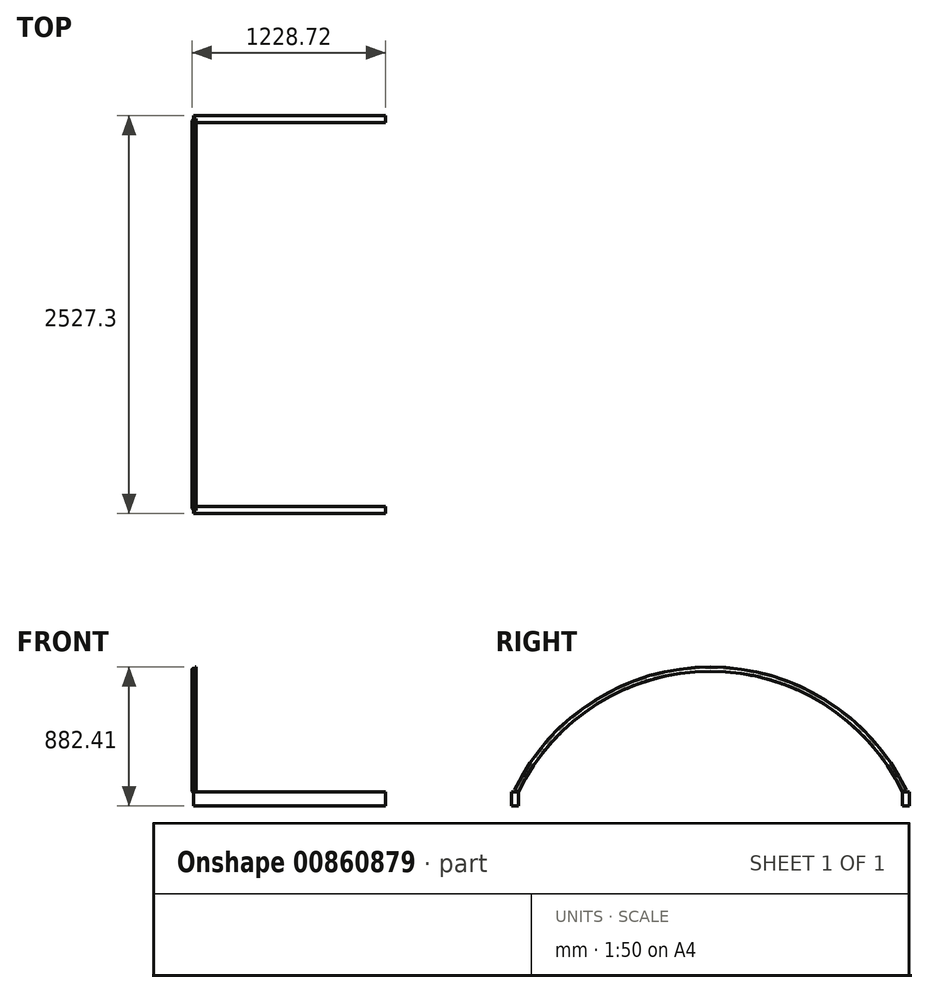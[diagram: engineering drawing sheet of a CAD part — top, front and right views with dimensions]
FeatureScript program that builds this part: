
annotation { "Feature Type Name" : "Feature", "Feature Type Description" : "" }
export const myFeature = defineFeature(function(context is Context, id is Id, definition is map)
    precondition{}
    {
        {
            var Q0;
            Q0=qCreatedBy(makeId("Top.planeOp"),FACE);
            var sketch = newSketch(context, id + "F0", { "sketchPlane" : qUnion([Q0])});
            skLineSegment(sketch, "E0", {"start": v(-3470.7, 1219.2) * mm, "end": v(-2251.5, 1219.2) * mm});
            skLineSegment(sketch, "E1.MirrorCS", {"start": v(-3470.7, -1219.2) * mm, "end": v(-2251.5, -1219.2) * mm});
            skLineSegment(sketch, "E2.0", {"start": v(-3470.7, 1263.65) * mm, "end": v(-2251.5, 1263.65) * mm});
            skLineSegment(sketch, "E3", {"start": v(-3470.7, 1219.2) * mm, "end": v(-3470.7, 1263.65) * mm});
            skLineSegment(sketch, "E4", {"start": v(-2251.5, 1219.2) * mm, "end": v(-2251.5, 1263.65) * mm});
            skLineSegment(sketch, "E5.MirrorCS", {"start": v(-3470.7, -1263.65) * mm, "end": v(-2251.5, -1263.65) * mm});
            skLineSegment(sketch, "E6.MirrorCS", {"start": v(-2251.5, -1219.2) * mm, "end": v(-2251.5, -1263.65) * mm});
            skLineSegment(sketch, "E7.MirrorCS", {"start": v(-3470.7, -1219.2) * mm, "end": v(-3470.7, -1263.65) * mm});
            skSolve(sketch);
        }
        {
            var Q0;
            Q0=makeQuery(id+"F0.imprint","IMPRINT",FACE,{"disambiguationData":[TD([[makeQuery(id+"F0.imprint","IMPRINT",EDGE,{"derivedFrom":sQuery(id+"F0.wireOp",EDGE,"E0")}),1.0]])]});
            var Q1;
            Q1=makeQuery(id+"F0.imprint","IMPRINT",FACE,{"disambiguationData":[TD([[makeQuery(id+"F0.imprint","IMPRINT",EDGE,{"derivedFrom":sQuery(id+"F0.wireOp",EDGE,"E1.MirrorCS")}),-1.0]])]});
            extrude(context, id + "F1", {"entities" : qUnion([Q0, Q1]), "depth" : 88.9 * mm, "offsetDistance" : 25.4 * mm});
        }
        {
            var Q0;
            Q0=makeQuery(id+"F1.opExtrude","SWEPT_FACE",FACE,{"disambiguationData":[OSD([sQuery(id+"F0.wireOp",EDGE,"E3")])]});
            var sketch = newSketch(context, id + "F2", { "sketchPlane" : qUnion([Q0])});
            skLineSegment(sketch, "E8.0.0", {"start": v(-1263.65, 0) * mm, "end": v(-1219.2, 0) * mm});
            skLineSegment(sketch, "E8.0.1", {"start": v(-1219.2, 0) * mm, "end": v(-1219.2, 88.9) * mm});
            skLineSegment(sketch, "E8.0.2", {"start": v(-1219.2, 88.9) * mm, "end": v(-1263.65, 88.9) * mm});
            skLineSegment(sketch, "E8.0.3", {"start": v(-1263.65, 88.9) * mm, "end": v(-1263.65, 0) * mm});
            skLineSegment(sketch, "E9.0.0", {"start": v(1219.2, 0) * mm, "end": v(1263.65, 0) * mm});
            skLineSegment(sketch, "E9.0.1", {"start": v(1263.65, 0) * mm, "end": v(1263.65, 88.9) * mm});
            skLineSegment(sketch, "E9.0.2", {"start": v(1263.65, 88.9) * mm, "end": v(1219.2, 88.9) * mm});
            skLineSegment(sketch, "E9.0.3", {"start": v(1219.2, 88.9) * mm, "end": v(1219.2, 0) * mm});
            skArc(sketch, "E10", {"start": v(1219.2, 88.9) * mm, "mid": v(0, 855.1) * mm, "end": v(-1219.2, 88.9) * mm});
            skArc(sketch, "E11.0", {"start": v(1236.36, 97.16) * mm, "mid": v(0, 874.16) * mm, "end": v(-1236.36, 97.16) * mm});
            skLineSegment(sketch, "E12", {"start": v(-1236.36, 97.16) * mm, "end": v(-1219.2, 88.9) * mm});
            skLineSegment(sketch, "E13", {"start": v(1236.36, 97.16) * mm, "end": v(1219.2, 88.9) * mm});
            skSolve(sketch);
        }
        {
            var Q0;
            Q0=sQuery(id+"F2.wireOp",EDGE,"E12");
            cPlane(context, id + "F3", {"entities" : qUnion([Q0]), "cplaneType" : CPlaneType.LINE_ANGLE, "offset" : 25.4 * mm, "angle" : 0 * degree, "width" : 152.4 * mm, "height" : 152.4 * mm});
        }
        {
            var Q0;
            Q0=qCreatedBy(id+"F3.planeOp",FACE);
            var sketch = newSketch(context, id + "F4", { "sketchPlane" : qUnion([Q0])});
            skLineSegment(sketch, "E14.0", {"start": v(-3470.7, -1156.15) * mm, "end": v(-3470.7, -1137.1) * mm});
            skCircle(sketch, "E15", {"center": v(-3470.7, -1146.63) * mm, "radius": 9.53 * mm});
            skSolve(sketch);
        }
        {
            var Q0;
            {var subQ0=sQuery(id+"F4.wireOp",EDGE,"E14.0");Q0=makeQuery(id+"F4.imprint","IMPRINT",FACE,{"disambiguationData":[TD([[makeQuery(id+"F4.imprint","IMPRINT",EDGE,{"derivedFrom":subQ0}),1.0]])]});}
            var Q1;
            {var subQ0=sQuery(id+"F4.wireOp",EDGE,"E14.0");Q1=makeQuery(id+"F4.imprint","IMPRINT",FACE,{"disambiguationData":[TD([[makeQuery(id+"F4.imprint","IMPRINT",EDGE,{"derivedFrom":subQ0}),-1.0]])]});}
            var Q2;
            Q2=sQuery(id+"F2.wireOp",EDGE,"E11.0");
            sweep(context, id + "F5", {"profiles" : qUnion([Q0, Q1]), "path" : qUnion([Q2])});
        }
        {
            var Q0;
            Q0=makeQuery(id+"F2.imprint","IMPRINT",FACE,{"disambiguationData":[TD([[makeQuery(id+"F2.imprint","IMPRINT",EDGE,{"derivedFrom":sQuery(id+"F2.wireOp",EDGE,"E8.0.0")}),-1.0]])]});
            var sketch = newSketch(context, id + "F6", { "sketchPlane" : qUnion([Q0])});
            skLineSegment(sketch, "E16.1.0", {"start": v(1263.65, 88.9) * mm, "end": v(1219.2, 88.9) * mm});
            skLineSegment(sketch, "E16.1.1", {"start": v(1219.2, 88.9) * mm, "end": v(1219.2, 0) * mm});
            skLineSegment(sketch, "E16.1.2", {"start": v(1219.2, 0) * mm, "end": v(1263.65, 0) * mm});
            skLineSegment(sketch, "E16.1.3", {"start": v(1263.65, 0) * mm, "end": v(1263.65, 88.9) * mm});
            skArc(sketch, "E17.0", {"start": v(1236.36, 97.16) * mm, "mid": v(0, 874.16) * mm, "end": v(-1236.36, 97.16) * mm});
            skLineSegment(sketch, "E18", {"start": v(-1259.25, 108.18) * mm, "end": v(-1236.36, 97.16) * mm});
            skLineSegment(sketch, "E19", {"start": v(0, -498) * mm, "end": v(0, 1228.3) * mm, "construction": true});
            skLineSegment(sketch, "E20.anchor1", {"start": v(0, -498) * mm, "end": v(0, 899.56) * mm, "construction": true});
            skLineSegment(sketch, "E21", {"start": v(0, -498) * mm, "end": v(-1259.25, 108.18) * mm, "construction": true});
            skLineSegment(sketch, "E22", {"start": v(0, -498) * mm, "end": v(1259.25, 108.18) * mm, "construction": true});
            skLineSegment(sketch, "E23", {"start": v(1259.25, 108.18) * mm, "end": v(1236.36, 97.16) * mm});
            skLineSegment(sketch, "E24", {"start": v(0, -498) * mm, "end": v(-316.78, 1194.72) * mm, "construction": true});
            skLineSegment(sketch, "E25.MirrorCS", {"start": v(0, -498) * mm, "end": v(316.78, 1194.72) * mm, "construction": true});
            skLineSegment(sketch, "E26.MirrorCS", {"start": v(0, -498) * mm, "end": v(624.27, 1111.48) * mm, "construction": true});
            skLineSegment(sketch, "E27.MirrorCS", {"start": v(0, -498) * mm, "end": v(907.47, 965.6) * mm, "construction": true});
            skLineSegment(sketch, "E28.MirrorCS", {"start": v(0, -498) * mm, "end": v(1164.05, 776.8) * mm, "construction": true});
            skLineSegment(sketch, "E29.MirrorCS", {"start": v(0, -498) * mm, "end": v(1375.33, 538.39) * mm, "construction": true});
            skLineSegment(sketch, "E30.MirrorCS", {"start": v(0, -498) * mm, "end": v(-624.27, 1111.48) * mm, "construction": true});
            skLineSegment(sketch, "E31.MirrorCS", {"start": v(0, -498) * mm, "end": v(-907.47, 965.6) * mm, "construction": true});
            skLineSegment(sketch, "E32.MirrorCS", {"start": v(0, -498) * mm, "end": v(-1164.05, 776.8) * mm, "construction": true});
            skLineSegment(sketch, "E33.MirrorCS", {"start": v(0, -498) * mm, "end": v(-1375.33, 538.39) * mm, "construction": true});
            skLineSegment(sketch, "E34", {"start": v(-257.08, 875.7) * mm, "end": v(-252.41, 850.74) * mm});
            skLineSegment(sketch, "E35", {"start": v(-505.4, 804.98) * mm, "end": v(-496.2, 781.3) * mm});
            skLineSegment(sketch, "E36", {"start": v(-736.45, 689.78) * mm, "end": v(-723.07, 668.19) * mm});
            skLineSegment(sketch, "E37", {"start": v(-942.38, 534.03) * mm, "end": v(-925.25, 515.28) * mm});
            skLineSegment(sketch, "E38", {"start": v(-1116.14, 343.07) * mm, "end": v(-1098.7, 323.98) * mm});
            skLineSegment(sketch, "E39", {"start": v(257.08, 875.7) * mm, "end": v(252.41, 850.74) * mm});
            skLineSegment(sketch, "E40", {"start": v(505.4, 804.98) * mm, "end": v(496.2, 781.3) * mm});
            skLineSegment(sketch, "E41", {"start": v(736.45, 689.78) * mm, "end": v(723.07, 668.19) * mm});
            skLineSegment(sketch, "E42", {"start": v(942.38, 534.03) * mm, "end": v(925.25, 515.28) * mm});
            skLineSegment(sketch, "E43", {"start": v(1116.14, 343.07) * mm, "end": v(1095.85, 327.79) * mm});
            skLineSegment(sketch, "E44", {"start": v(0, 874.16) * mm, "end": v(0, 899.56) * mm});
            skSolve(sketch);
        }
        {
            var Q0;
            Q0=qCreatedBy(id+"F3.planeOp",FACE);
            var sketch = newSketch(context, id + "F7", { "sketchPlane" : qUnion([Q0])});
            skLineSegment(sketch, "E45", {"start": v(-3461.17, 1065.93) * mm, "end": v(-3461.17, -1146.63) * mm});
            skArc(sketch, "E46", {"start": v(-3461.17, -1146.63) * mm, "mid": v(-3470.7, -1137.1) * mm, "end": v(-3480.22, -1146.63) * mm});
            skLineSegment(sketch, "E47.bottom", {"start": v(-3461.17, -1137.1) * mm, "end": v(-3454.82, -1137.1) * mm});
            skLineSegment(sketch, "E47.top", {"start": v(-3461.17, -1164.4) * mm, "end": v(-3454.82, -1164.4) * mm});
            skLineSegment(sketch, "E47.left", {"start": v(-3461.17, -1137.1) * mm, "end": v(-3461.17, -1164.4) * mm});
            skLineSegment(sketch, "E47.right", {"start": v(-3454.82, -1137.1) * mm, "end": v(-3454.82, -1164.4) * mm});
            skSolve(sketch);
        }
        {
            var Q0;
            {var subQ3=sQuery(id+"F7.wireOp",EDGE,"E47.bottom");Q0=makeQuery(id+"F7.imprint","IMPRINT",FACE,{"disambiguationData":[TD([[makeQuery(id+"F7.imprint","IMPRINT",EDGE,{"derivedFrom":subQ3}),-1.0]])]});}
            var Q1;
            Q1=sQuery(id+"F2.wireOp",EDGE,"E11.0");
            sweep(context, id + "F8", {"profiles" : qUnion([Q0]), "path" : qUnion([Q1])});
        }
    });
